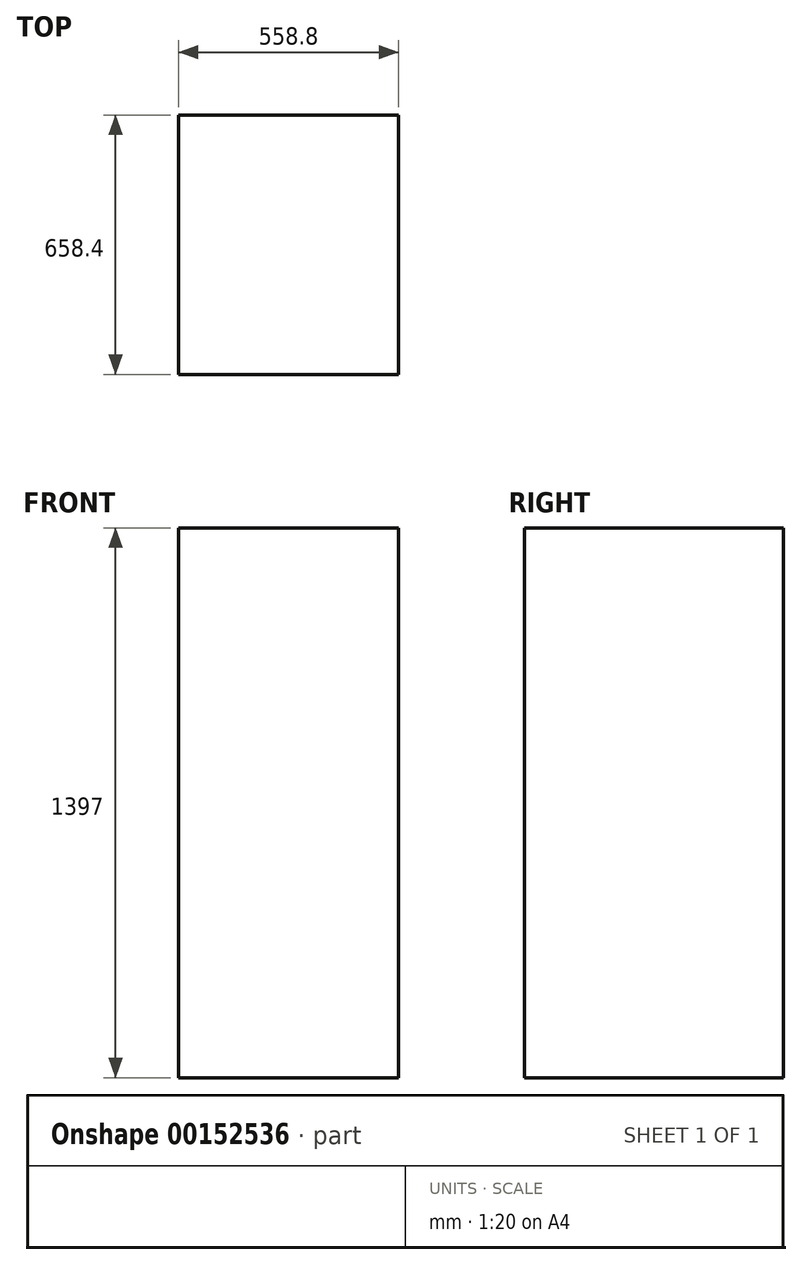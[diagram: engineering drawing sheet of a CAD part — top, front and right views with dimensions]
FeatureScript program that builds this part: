
annotation { "Feature Type Name" : "Feature", "Feature Type Description" : "" }
export const myFeature = defineFeature(function(context is Context, id is Id, definition is map)
    precondition{}
    {
        {
            var Q0;
            Q0=qCreatedBy(makeId("Front.planeOp"),FACE);
            var sketch = newSketch(context, id + "F0", { "sketchPlane" : qUnion([Q0])});
            skLineSegment(sketch, "E0.bottom", {"start": v(0, 0) * mm, "end": v(558.8, 0) * mm});
            skLineSegment(sketch, "E0.top", {"start": v(0, 1397) * mm, "end": v(558.8, 1397) * mm});
            skLineSegment(sketch, "E0.left", {"start": v(0, 0) * mm, "end": v(0, 1397) * mm});
            skLineSegment(sketch, "E0.right", {"start": v(558.8, 0) * mm, "end": v(558.8, 1397) * mm});
            skSolve(sketch);
        }
        {
            var Q0;
            Q0=makeQuery(id+"F0.imprint","IMPRINT",FACE,{"disambiguationData":[TD([[makeQuery(id+"F0.imprint","IMPRINT",EDGE,{"derivedFrom":sQuery(id+"F0.wireOp",EDGE,"E0.bottom")}),1.0]])]});
            extrude(context, id + "F1", {"entities" : qUnion([Q0]), "depth" : 658.4 * mm});
        }
    });
